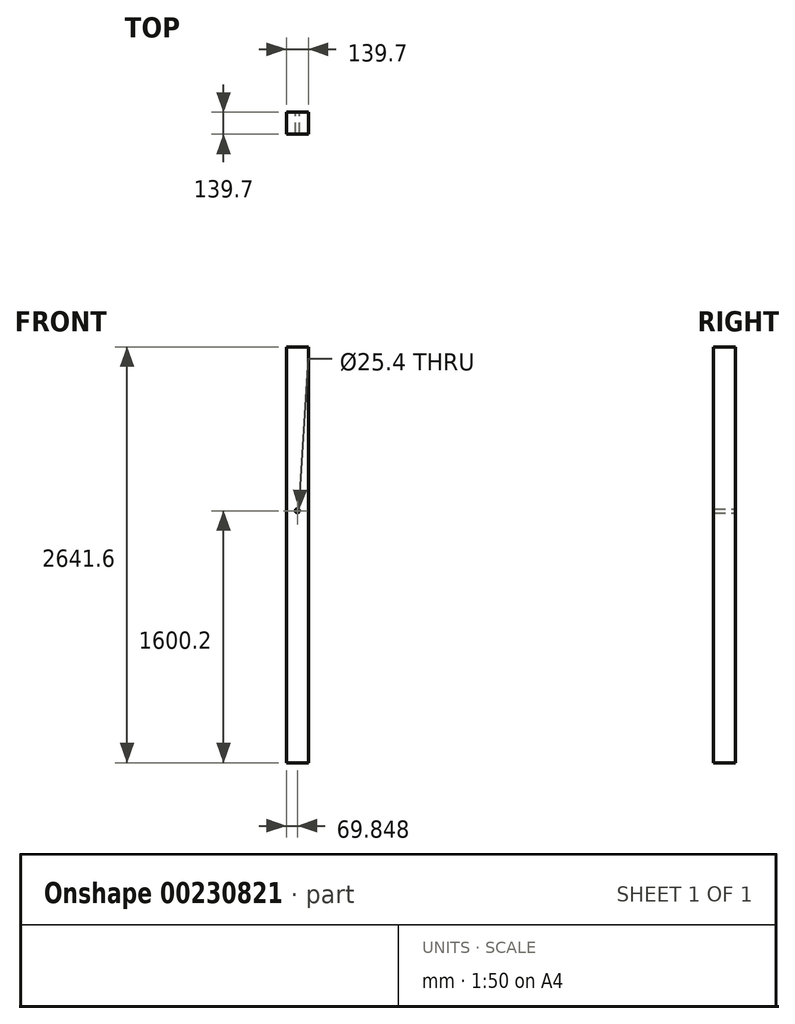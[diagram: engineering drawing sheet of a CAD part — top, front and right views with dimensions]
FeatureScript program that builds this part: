
annotation { "Feature Type Name" : "Feature", "Feature Type Description" : "" }
export const myFeature = defineFeature(function(context is Context, id is Id, definition is map)
    precondition{}
    {
        {
            var Q0;
            Q0=qCreatedBy(makeId("Front.planeOp"),FACE);
            var sketch = newSketch(context, id + "F0", { "sketchPlane" : qUnion([Q0])});
            skLineSegment(sketch, "E0.bottom", {"start": v(-186.95, 1314.42) * mm, "end": v(-47.25, 1314.42) * mm});
            skLineSegment(sketch, "E0.top", {"start": v(-186.95, -1327.18) * mm, "end": v(-47.25, -1327.18) * mm});
            skLineSegment(sketch, "E0.left", {"start": v(-186.95, 1314.42) * mm, "end": v(-186.95, -1327.18) * mm});
            skLineSegment(sketch, "E0.right", {"start": v(-47.25, 1314.42) * mm, "end": v(-47.25, -1327.18) * mm});
            skCircle(sketch, "E1", {"center": v(-117.1, 273.02) * mm, "radius": 12.7 * mm});
            skSolve(sketch);
        }
        {
            var Q0;
            Q0 = qSketchRegion(id + "F0", true);
            var Q1;
            Q1=makeQuery(id+"F0.imprint","IMPRINT",FACE,{"disambiguationData":[TD([[makeQuery(id+"F0.imprint","IMPRINT",EDGE,{"derivedFrom":sQuery(id+"F0.wireOp",EDGE,"E0.bottom")}),-1.0]])]});
            extrude(context, id + "F1", {"entities" : qUnion([Q0, Q1]), "depth" : 139.7 * mm});
        }
    });
